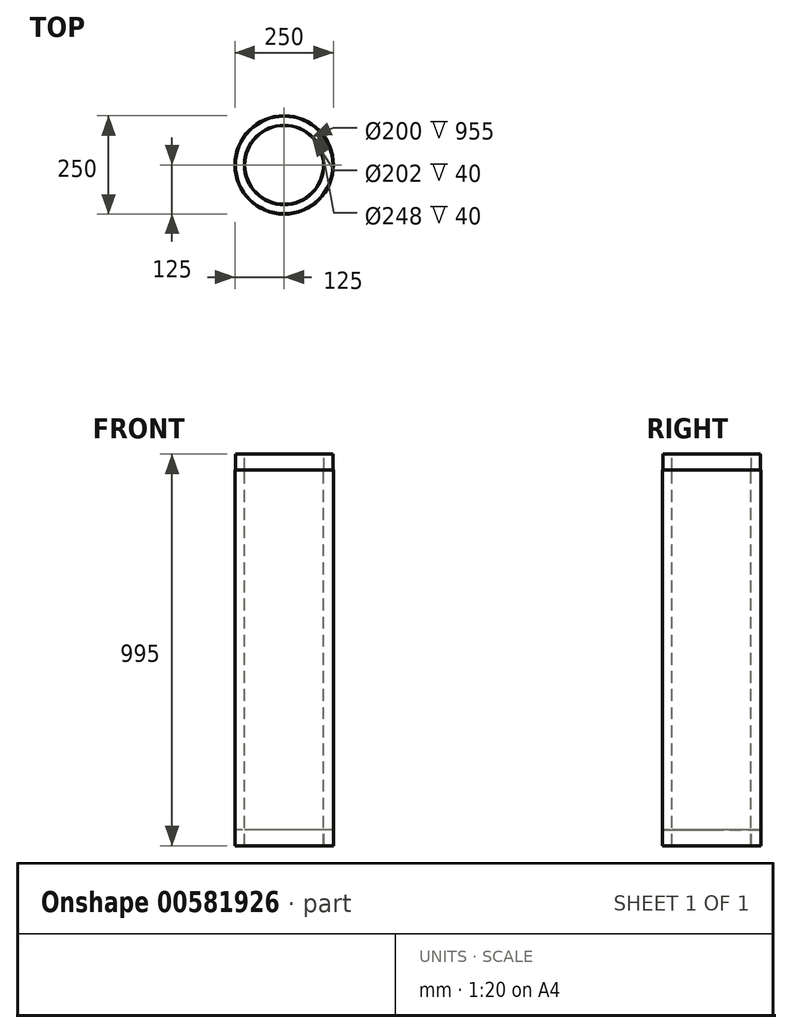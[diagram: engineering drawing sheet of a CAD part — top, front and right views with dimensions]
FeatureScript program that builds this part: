
annotation { "Feature Type Name" : "Feature", "Feature Type Description" : "" }
export const myFeature = defineFeature(function(context is Context, id is Id, definition is map)
    precondition{}
    {
        {
            var Q0;
            Q0=qCreatedBy(makeId("Front.planeOp"),FACE);
            var sketch = newSketch(context, id + "F0", { "sketchPlane" : qUnion([Q0])});
            skLineSegment(sketch, "E0", {"start": v(0, 345.75) * mm, "end": v(0, -558.03) * mm, "construction": true});
            skLineSegment(sketch, "E1", {"start": v(-100, -518.84) * mm, "end": v(-100, 436.16) * mm});
            skLineSegment(sketch, "E2", {"start": v(-100, 436.16) * mm, "end": v(-101, 436.16) * mm});
            skLineSegment(sketch, "E3", {"start": v(-101, 436.16) * mm, "end": v(-101, 476.16) * mm});
            skLineSegment(sketch, "E4", {"start": v(-101, 476.16) * mm, "end": v(-124, 476.16) * mm});
            skLineSegment(sketch, "E5", {"start": v(-124, 476.16) * mm, "end": v(-124, 436.16) * mm});
            skLineSegment(sketch, "E6", {"start": v(-124, 436.16) * mm, "end": v(-125, 436.16) * mm});
            skLineSegment(sketch, "E7", {"start": v(-125, 436.16) * mm, "end": v(-125, -518.84) * mm});
            skLineSegment(sketch, "E8", {"start": v(-125, -518.84) * mm, "end": v(-124, -518.84) * mm});
            skLineSegment(sketch, "E9", {"start": v(-124, -518.84) * mm, "end": v(-124, -478.84) * mm});
            skLineSegment(sketch, "E10", {"start": v(-124, -478.84) * mm, "end": v(-101, -478.84) * mm});
            skLineSegment(sketch, "E11", {"start": v(-101, -478.84) * mm, "end": v(-101, -518.84) * mm});
            skLineSegment(sketch, "E12", {"start": v(-101, -518.84) * mm, "end": v(-100, -518.84) * mm});
            skSolve(sketch);
        }
        {
            var Q0;
            Q0=qSketchRegion(id+"F0",true);
            var Q1;
            Q1=sQuery(id+"F0.wireOp",EDGE,"E0");
            revolve(context, id + "F1", {"entities" : qUnion([Q0]), "axis" : qUnion([Q1]), "revolveType" : RevolveType.FULL});
        }
    });
